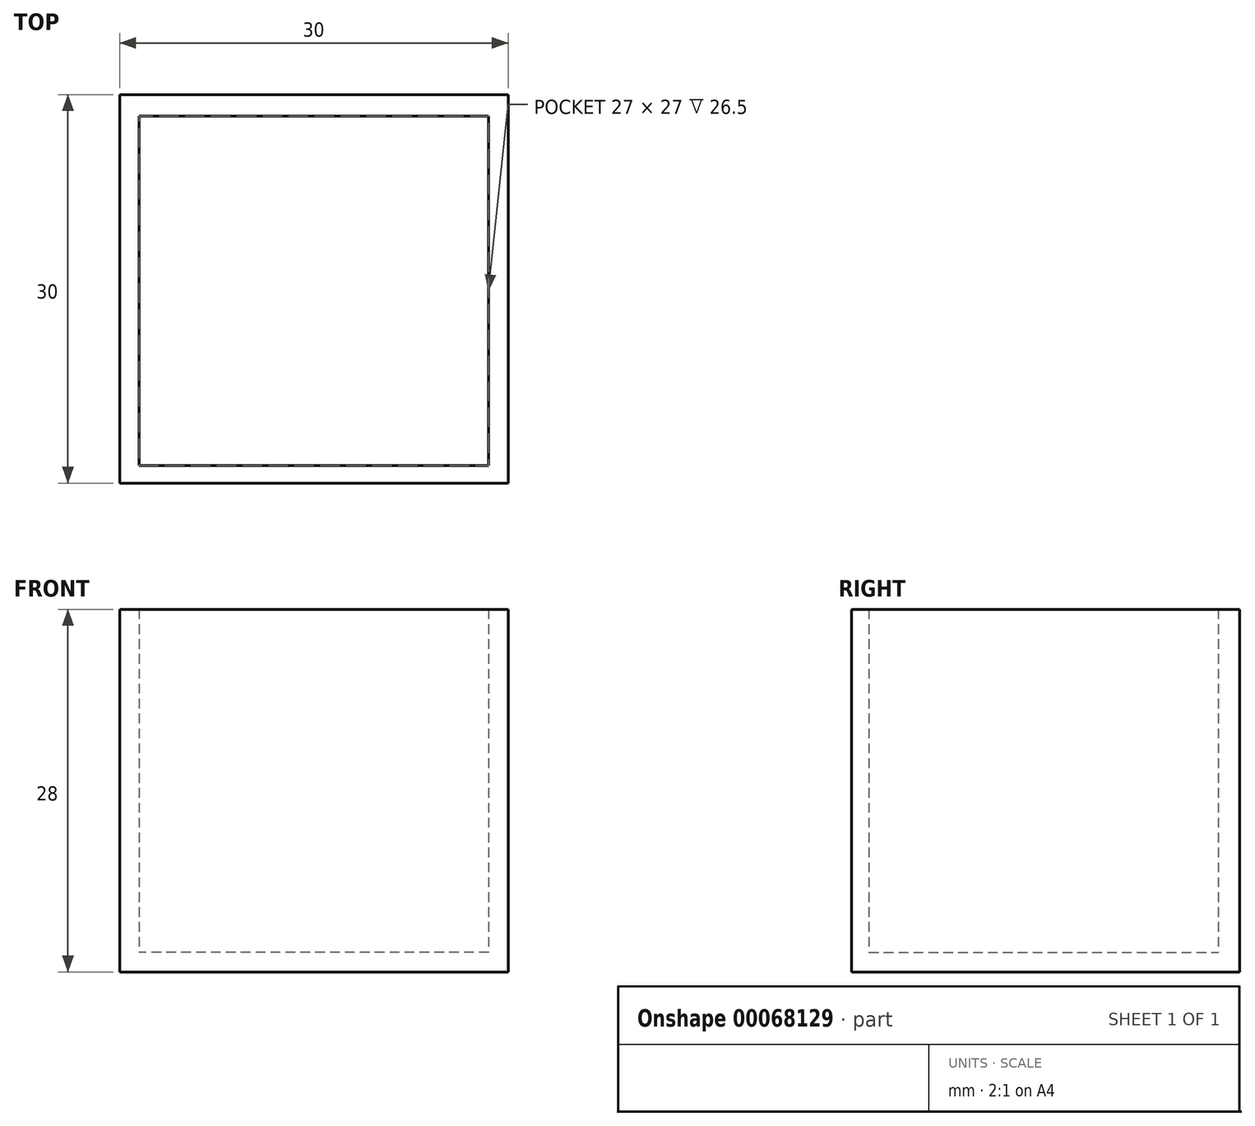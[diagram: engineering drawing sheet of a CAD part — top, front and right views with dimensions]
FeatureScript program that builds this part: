
annotation { "Feature Type Name" : "Feature", "Feature Type Description" : "" }
export const myFeature = defineFeature(function(context is Context, id is Id, definition is map)
    precondition{}
    {
        {
            var Q0;
            Q0=qCreatedBy(makeId("Top.planeOp"),FACE);
            var sketch = newSketch(context, id + "F0", { "sketchPlane" : qUnion([Q0])});
            skLineSegment(sketch, "E0.bottom", {"start": v(-14.92, 14.9) * mm, "end": v(15.08, 14.9) * mm});
            skLineSegment(sketch, "E0.top", {"start": v(-14.92, -15.1) * mm, "end": v(15.08, -15.1) * mm});
            skLineSegment(sketch, "E0.left", {"start": v(-14.92, 14.9) * mm, "end": v(-14.92, -15.1) * mm});
            skLineSegment(sketch, "E0.right", {"start": v(15.08, 14.9) * mm, "end": v(15.08, -15.1) * mm});
            skLineSegment(sketch, "E1.bottom", {"start": v(-13.42, 13.24) * mm, "end": v(13.58, 13.24) * mm});
            skLineSegment(sketch, "E1.top", {"start": v(-13.42, -13.76) * mm, "end": v(13.58, -13.76) * mm});
            skLineSegment(sketch, "E1.left", {"start": v(-13.42, 13.24) * mm, "end": v(-13.42, -13.76) * mm});
            skLineSegment(sketch, "E1.right", {"start": v(13.58, 13.24) * mm, "end": v(13.58, -13.76) * mm});
            skSolve(sketch);
        }
        {
            var Q0;
            Q0 = qSketchRegion(id + "F0", true);
            var Q1;
            Q1=makeQuery(id+"F0.imprint","IMPRINT",FACE,{"disambiguationData":[TD([[makeQuery(id+"F0.imprint","IMPRINT",EDGE,{"derivedFrom":sQuery(id+"F0.wireOp",EDGE,"E1.bottom")}),-1.0]])]});
            extrude(context, id + "F1", {"entities" : qUnion([Q0, Q1]), "depth" : 1.5 * mm});
        }
        {
            var Q0;
            Q0 = qSketchRegion(id + "F0", true);
            extrude(context, id + "F2", {"entities" : qUnion([Q0]), "operationType" : NewBodyOperationType.ADD, "depth" : 28 * mm});
        }
    });
